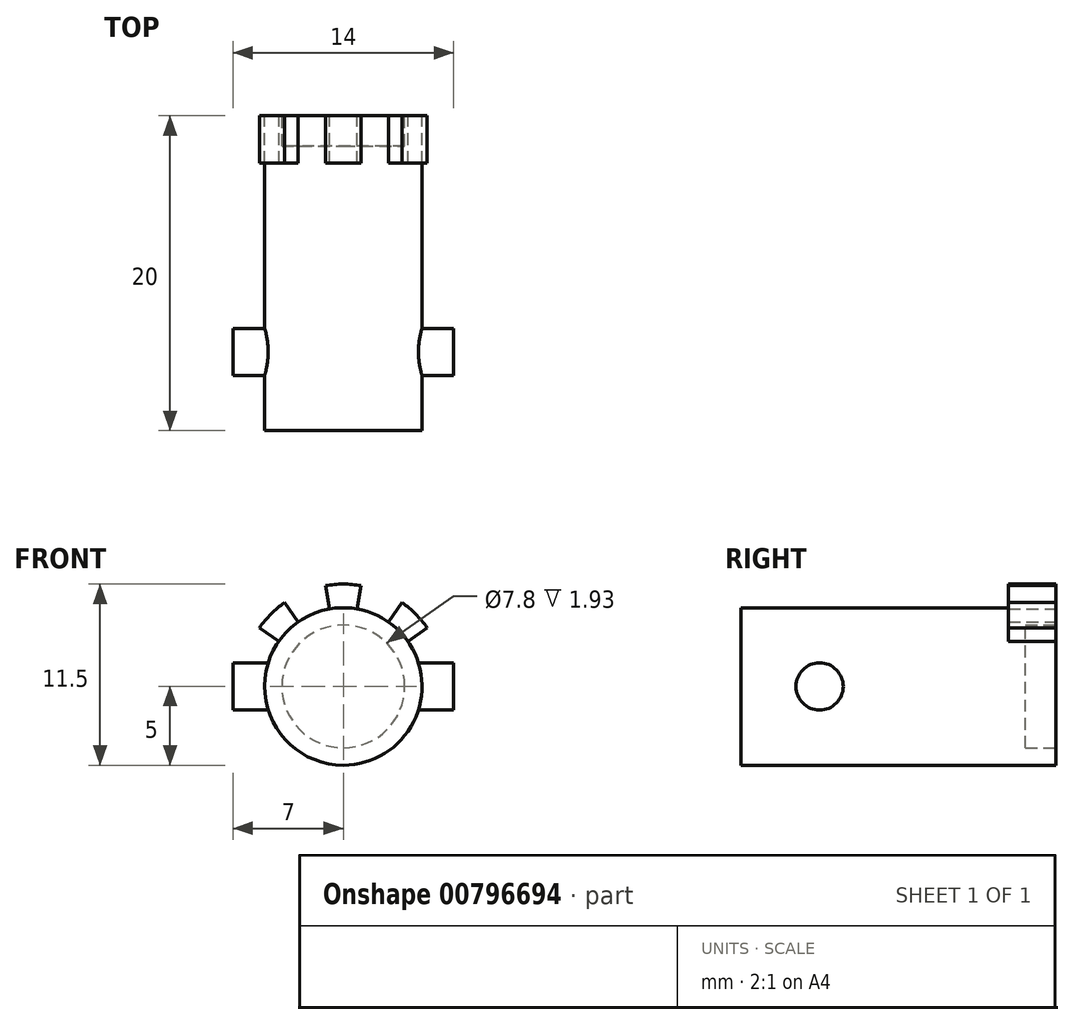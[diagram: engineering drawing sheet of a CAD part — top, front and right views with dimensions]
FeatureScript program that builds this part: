
annotation { "Feature Type Name" : "Feature", "Feature Type Description" : "" }
export const myFeature = defineFeature(function(context is Context, id is Id, definition is map)
    precondition{}
    {
        {
            var Q0;
            Q0=qCreatedBy(makeId("Front.planeOp"),FACE);
            var sketch = newSketch(context, id + "F0", { "sketchPlane" : qUnion([Q0])});
            skCircle(sketch, "E0", {"center": v(0, 0) * mm, "radius": 3.9 * mm});
            skCircle(sketch, "E1", {"center": v(0, 0) * mm, "radius": 5 * mm});
            skLineSegment(sketch, "E2", {"start": v(0, 0) * mm, "end": v(0, 3.9) * mm});
            skLineSegment(sketch, "E3", {"start": v(0, 0) * mm, "end": v(5, 0) * mm});
            skLineSegment(sketch, "E4", {"start": v(0, 0) * mm, "end": v(0, 5) * mm});
            skLineSegment(sketch, "E5", {"start": v(0, 0) * mm, "end": v(-5, 0) * mm});
            skLineSegment(sketch, "E6", {"start": v(0, 0) * mm, "end": v(3.54, 3.54) * mm});
            skLineSegment(sketch, "E7", {"start": v(0, 0) * mm, "end": v(-3.54, 3.54) * mm});
            skCircle(sketch, "E8", {"center": v(0, 0) * mm, "radius": 6.5 * mm});
            skLineSegment(sketch, "E9", {"start": v(0, 0) * mm, "end": v(4.1, 2.87) * mm});
            skLineSegment(sketch, "E10", {"start": v(0, 0) * mm, "end": v(2.87, 4.1) * mm});
            skLineSegment(sketch, "E11", {"start": v(0, 0) * mm, "end": v(0.87, 4.92) * mm});
            skLineSegment(sketch, "E12", {"start": v(0, 0) * mm, "end": v(-0.87, 4.92) * mm});
            skLineSegment(sketch, "E13", {"start": v(0, 0) * mm, "end": v(-2.87, 4.1) * mm});
            skLineSegment(sketch, "E14", {"start": v(0, 0) * mm, "end": v(-4.1, 2.87) * mm});
            skLineSegment(sketch, "E15", {"start": v(4.1, 2.87) * mm, "end": v(5.32, 3.73) * mm});
            skLineSegment(sketch, "E16", {"start": v(2.87, 4.1) * mm, "end": v(3.73, 5.32) * mm});
            skLineSegment(sketch, "E17", {"start": v(0.87, 4.92) * mm, "end": v(1.13, 6.4) * mm});
            skLineSegment(sketch, "E18", {"start": v(-0.87, 4.92) * mm, "end": v(-1.13, 6.4) * mm});
            skLineSegment(sketch, "E19", {"start": v(-2.87, 4.1) * mm, "end": v(-3.73, 5.32) * mm});
            skLineSegment(sketch, "E20", {"start": v(-4.1, 2.87) * mm, "end": v(-5.32, 3.73) * mm});
            skSolve(sketch);
        }
        {
            var Q0;
            Q0=makeQuery(id+"F0.imprint","IMPRINT",FACE,{"disambiguationData":[TD([[makeQuery(id+"F0.imprint","IMPRINT",EDGE,{"derivedFrom":sQuery(id+"F0.wireOp",EDGE,"E0")}),1.0]])]});
            var Q1;
            Q1=makeQuery(id+"F0.imprint","IMPRINT",FACE,{"disambiguationData":[TD([[makeQuery(id+"F0.imprint","IMPRINT",EDGE,{"derivedFrom":sQuery(id+"F0.wireOp",EDGE,"E0")}),-1.0]])]});
            extrude(context, id + "F1", {"entities" : qUnion([Q0, Q1]), "depth" : 20 * mm, "offsetDistance" : 25 * mm});
        }
        {
            var Q0;
            Q0=makeQuery(id+"F0.imprint","IMPRINT",FACE,{"disambiguationData":[TD([[makeQuery(id+"F0.imprint","IMPRINT",EDGE,{"derivedFrom":sQuery(id+"F0.wireOp",EDGE,"E0")}),1.0]])]});
            extrude(context, id + "F2", {"entities" : qUnion([Q0]), "operationType" : NewBodyOperationType.REMOVE, "depth" : 1.93 * mm, "offsetDistance" : 25 * mm});
        }
        {
            var Q0;
            {var subQ0=sQuery(id+"F0.wireOp",EDGE,"E15");Q0=makeQuery(id+"F0.imprint","IMPRINT",FACE,{"disambiguationData":[TD([[makeQuery(id+"F0.imprint","IMPRINT",EDGE,{"derivedFrom":subQ0}),1.0]])]});}
            var Q1;
            {var subQ0=sQuery(id+"F0.wireOp",EDGE,"E17");Q1=makeQuery(id+"F0.imprint","IMPRINT",FACE,{"disambiguationData":[TD([[makeQuery(id+"F0.imprint","IMPRINT",EDGE,{"derivedFrom":subQ0}),1.0]])]});}
            var Q2;
            {var subQ0=sQuery(id+"F0.wireOp",EDGE,"E19");Q2=makeQuery(id+"F0.imprint","IMPRINT",FACE,{"disambiguationData":[TD([[makeQuery(id+"F0.imprint","IMPRINT",EDGE,{"derivedFrom":subQ0}),1.0]])]});}
            extrude(context, id + "F3", {"entities" : qUnion([Q0, Q1, Q2]), "operationType" : NewBodyOperationType.ADD, "depth" : 3 * mm, "offsetDistance" : 25 * mm});
        }
        {
            var Q0;
            Q0=qCreatedBy(makeId("Right.planeOp"),FACE);
            var sketch = newSketch(context, id + "F4", { "sketchPlane" : qUnion([Q0])});
            skLineSegment(sketch, "E21", {"start": v(0, 0) * mm, "end": v(-15, 0) * mm});
            skCircle(sketch, "E22", {"center": v(-15, 0) * mm, "radius": 1.5 * mm});
            skSolve(sketch);
        }
        {
            var Q0;
            Q0=makeQuery(id+"F4.imprint","IMPRINT",FACE,{"disambiguationData":[TD([[makeQuery(id+"F4.imprint","IMPRINT",EDGE,{"derivedFrom":sQuery(id+"F4.wireOp",EDGE,"E22")}),1.0]])]});
            extrude(context, id + "F5", {"entities" : qUnion([Q0]), "operationType" : NewBodyOperationType.ADD, "depth" : 7 * mm, "offsetDistance" : 25 * mm, "hasSecondDirection" : true, "secondDirectionOppositeDirection" : true, "secondDirectionDepth" : 7 * mm});
        }
    });
